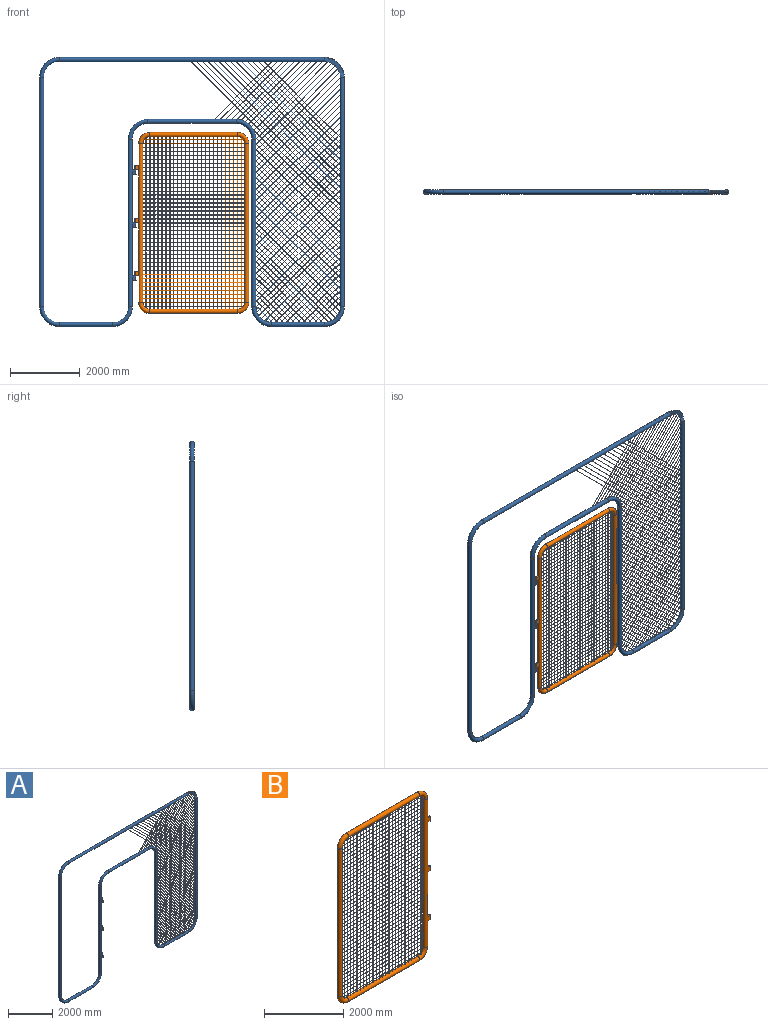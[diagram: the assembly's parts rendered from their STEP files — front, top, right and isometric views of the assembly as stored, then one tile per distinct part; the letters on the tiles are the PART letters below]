
ASSEMBLY  parts=2 mates=1
PART A: 186 faces, bbox 8852.5x122.7x7836.5 mm
  f0: torus R=508mm, axis (0,-1,0), area 307549mm2, adj f1,f15
  f1: cylinder r=61.34mm len=1524mm, axis (1,0,0), area 587375.3mm2, adj f0,f2
  f2: torus R=508mm, axis (0,-1,0), area 307549mm2, adj f1,f3
  f3: cylinder r=61.34mm len=6604mm, axis (0,0,-1), area 2545293mm2, adj f2,f4
  f4: torus R=508mm, axis (0,-1,0), area 307549mm2, adj f3,f5
  f5: cylinder r=61.34mm len=7620mm, axis (-1,0,0), area 2935875.4mm2, adj f4,f6,f47,f48,f49,f50,f51,f52
  f6: torus R=508mm, axis (0,-1,0), area 307392.8mm2, adj f5,f7,f103,f104,f105,f106,f107
  f7: cylinder r=61.34mm len=6604mm, axis (0,0,1), area 2542310.5mm2, adj f6,f8,f30,f31,f32,f33,f34,f35
  f8: torus R=508mm, axis (0,-1,0), area 307391.4mm2, adj f7,f9,f25,f26,f27,f28,f29
  f9: cylinder r=61.34mm len=1524mm, axis (1,0,0), area 586591mm2, adj f8,f10,f16,f17,f18,f19,f20,f21
  f10: torus R=508mm, axis (0,-1,0), area 307350.3mm2, adj f9,f11,f62,f63,f64,f65,f66,f76
  f11: cylinder r=61.34mm len=4826mm, axis (0,0,-1), area 1857540.3mm2, adj f10,f12,f16,f17,f18,f19,f20,f21
  f12: torus R=508mm, axis (0,1,0), area 307176.7mm2, adj f11,f13,f45,f46,f107,f108,f109,f110
  f13: cylinder r=61.34mm len=2540mm, axis (1,0,0), area 978792.6mm2, adj f12,f14,f114,f115,f116,f117
  f14: torus R=508mm, axis (0,1,0), area 307549mm2, adj f13,f15
  f15: cylinder r=61.34mm len=4826mm, axis (0,0,1), area 1840066.3mm2, adj f0,f14,f118,f119,f120,f121,f124,f125
  f16: cylinder r=3.05mm len=640.63mm, axis (-0.71,0,0.71), area 17118.8mm2, adj f9,f11
  f17: cylinder r=3.05mm len=801.92mm, axis (-0.71,0,0.71), area 21487.2mm2, adj f9,f11
  f18: cylinder r=3.05mm len=963.21mm, axis (-0.71,0,0.71), area 25855.5mm2, adj f9,f11
  f19: cylinder r=3.05mm len=1124.5mm, axis (-0.71,0,0.71), area 30223.9mm2, adj f9,f11
  f20: cylinder r=3.05mm len=1285.79mm, axis (-0.71,0,0.71), area 34592.2mm2, adj f9,f11
  f21: cylinder r=3.05mm len=1447.08mm, axis (-0.71,0,0.71), area 38960.6mm2, adj f9,f11
  f22: cylinder r=3.05mm len=1608.37mm, axis (-0.71,0,0.71), area 43328.9mm2, adj f9,f11
  f23: cylinder r=3.05mm len=1769.66mm, axis (-0.71,0,0.71), area 47697.3mm2, adj f9,f11
  f24: cylinder r=3.05mm len=1930.95mm, axis (-0.71,0,0.71), area 52065.6mm2, adj f9,f11
  f25: cylinder r=3.05mm len=2079.79mm, axis (-0.71,0,0.71), area 56118.8mm2, adj f8,f11
  f26: cylinder r=3.05mm len=2195.41mm, axis (-0.71,0,0.71), area 59269.8mm2, adj f8,f11
  f27: cylinder r=3.05mm len=2287.57mm, axis (-0.71,0,0.71), area 61777.9mm2, adj f8,f11
  f28: cylinder r=3.05mm len=2359.6mm, axis (-0.71,0,0.71), area 63718.8mm2, adj f8,f11
  f29: cylinder r=3.05mm len=2408.95mm, axis (-0.71,0,0.71), area 65037.1mm2, adj f8,f11
  f30: cylinder r=3.05mm len=2426.1mm, axis (-0.71,0,0.71), area 65476.3mm2, adj f7,f11
  f31: cylinder r=3.05mm len=2426.1mm, axis (-0.71,0,0.71), area 65476.3mm2, adj f7,f11
  f32: cylinder r=3.05mm len=2426.1mm, axis (-0.71,0,0.71), area 65476.3mm2, adj f7,f11
  f33: cylinder r=3.05mm len=2426.1mm, axis (-0.71,0,0.71), area 65476.3mm2, adj f7,f11
  f34: cylinder r=3.05mm len=2426.1mm, axis (-0.71,0,0.71), area 65476.3mm2, adj f7,f11
  f35: cylinder r=3.05mm len=2426.1mm, axis (-0.71,0,0.71), area 65476.3mm2, adj f7,f11
  f36: cylinder r=3.05mm len=2426.1mm, axis (-0.71,0,0.71), area 65476.3mm2, adj f7,f11
  f37: cylinder r=3.05mm len=2426.1mm, axis (-0.71,0,0.71), area 65476.3mm2, adj f7,f11
  f38: cylinder r=3.05mm len=2426.1mm, axis (-0.71,0,0.71), area 65476.3mm2, adj f7,f11
  f39: cylinder r=3.05mm len=2426.1mm, axis (-0.71,0,0.71), area 65476.3mm2, adj f7,f11
  f40: cylinder r=3.05mm len=2426.1mm, axis (-0.71,0,0.71), area 65476.3mm2, adj f7,f11
  f41: cylinder r=3.05mm len=2426.1mm, axis (-0.71,0,0.71), area 65476.3mm2, adj f7,f11
  f42: cylinder r=3.05mm len=2426.1mm, axis (-0.71,0,0.71), area 65476.3mm2, adj f7,f11
  f43: cylinder r=3.05mm len=2426.1mm, axis (-0.71,0,0.71), area 65476.3mm2, adj f7,f11
  f44: cylinder r=3.05mm len=2426.1mm, axis (-0.71,0,0.71), area 65476.3mm2, adj f7,f11
  f45: cylinder r=3.05mm len=2427.7mm, axis (-0.71,0,0.71), area 65511mm2, adj f7,f12
  f46: cylinder r=3.05mm len=2494.65mm, axis (-0.71,0,0.71), area 67205.7mm2, adj f7,f12
  f47: cylinder r=3.05mm len=4291.59mm, axis (-0.71,0,0.71), area 116000.9mm2, adj f5,f7
  f48: cylinder r=3.05mm len=4130.3mm, axis (-0.71,0,0.71), area 111632.5mm2, adj f5,f7
  f49: cylinder r=3.05mm len=3969.01mm, axis (-0.71,0,0.71), area 107264.2mm2, adj f5,f7
  f50: cylinder r=3.05mm len=3807.72mm, axis (-0.71,0,0.71), area 102895.8mm2, adj f5,f7
  f51: cylinder r=3.05mm len=3646.43mm, axis (-0.71,0,0.71), area 98527.5mm2, adj f5,f7
  f52: cylinder r=3.05mm len=3485.14mm, axis (-0.71,0,0.71), area 94159.1mm2, adj f5,f7
  f53: cylinder r=3.05mm len=3323.85mm, axis (-0.71,0,0.71), area 89790.8mm2, adj f5,f7
  f54: cylinder r=3.05mm len=3162.56mm, axis (-0.71,0,0.71), area 85422.4mm2, adj f5,f7
  f55: cylinder r=3.05mm len=3001.27mm, axis (-0.71,0,0.71), area 81054.1mm2, adj f5,f7
  f56: cylinder r=3.05mm len=2839.98mm, axis (-0.71,0,0.71), area 76685.7mm2, adj f5,f7
  f57: cylinder r=3.05mm len=2678.69mm, axis (-0.71,0,0.71), area 72317.4mm2, adj f5,f7
  f58: cylinder r=3.05mm len=2517.4mm, axis (-0.71,0,0.71), area 67949mm2, adj f5,f7
  f59: cylinder r=3.05mm len=2356.11mm, axis (-0.71,0,0.71), area 63580.7mm2, adj f5,f7
  f60: cylinder r=3.05mm len=2194.82mm, axis (-0.71,0,0.71), area 59212.3mm2, adj f5,f7
  f61: cylinder r=3.05mm len=479.34mm, axis (-0.71,0,0.71), area 12750.5mm2, adj f9,f11
  f62: cylinder r=3.05mm len=2396.51mm, axis (-0.71,0,-0.71), area 64706.6mm2, adj f7,f10
  f63: cylinder r=3.05mm len=2339.58mm, axis (-0.71,0,-0.71), area 63181.2mm2, adj f7,f10
  f64: cylinder r=3.05mm len=2261.34mm, axis (-0.71,0,-0.71), area 61065.2mm2, adj f7,f10
  f65: cylinder r=3.05mm len=2162.52mm, axis (-0.71,0,-0.71), area 58373.6mm2, adj f7,f10
  f66: cylinder r=3.05mm len=2038mm, axis (-0.71,0,-0.71), area 54978.7mm2, adj f7,f10
  f67: cylinder r=3.05mm len=1881.16mm, axis (-0.71,0,-0.71), area 50717.1mm2, adj f7,f9
  f68: cylinder r=3.05mm len=1719.87mm, axis (-0.71,0,-0.71), area 46348.7mm2, adj f7,f9
  f69: cylinder r=3.05mm len=1558.58mm, axis (-0.71,0,-0.71), area 41980.4mm2, adj f7,f9
  f70: cylinder r=3.05mm len=1397.29mm, axis (-0.71,0,-0.71), area 37612mm2, adj f7,f9
  f71: cylinder r=3.05mm len=1236mm, axis (-0.71,0,-0.71), area 33243.7mm2, adj f7,f9
  f72: cylinder r=3.05mm len=1074.71mm, axis (-0.71,0,-0.71), area 28875.4mm2, adj f7,f9
  f73: cylinder r=3.05mm len=913.42mm, axis (-0.71,0,-0.71), area 24507mm2, adj f7,f9
  f74: cylinder r=3.05mm len=752.13mm, axis (-0.71,0,-0.71), area 20138.7mm2, adj f7,f9
  f75: cylinder r=3.05mm len=590.84mm, axis (-0.71,0,-0.71), area 15770.3mm2, adj f7,f9
  f76: cylinder r=3.05mm len=2425.29mm, axis (-0.71,0,-0.71), area 65460.2mm2, adj f7,f10
  f77: cylinder r=3.05mm len=2426.13mm, axis (-0.71,0,-0.71), area 65477.1mm2, adj f7,f11
  f78: cylinder r=3.05mm len=2426.13mm, axis (-0.71,0,-0.71), area 65477.1mm2, adj f7,f11
  f79: cylinder r=3.05mm len=2426.13mm, axis (-0.71,0,-0.71), area 65477.1mm2, adj f7,f11
  f80: cylinder r=3.05mm len=2426.13mm, axis (-0.71,0,-0.71), area 65477.1mm2, adj f7,f11
  f81: cylinder r=3.05mm len=2426.13mm, axis (-0.71,0,-0.71), area 65477.1mm2, adj f7,f11
  f82: cylinder r=3.05mm len=2426.13mm, axis (-0.71,0,-0.71), area 65477.1mm2, adj f7,f11
  f83: cylinder r=3.05mm len=2426.13mm, axis (-0.71,0,-0.71), area 65477.1mm2, adj f7,f11
  f84: cylinder r=3.05mm len=2426.13mm, axis (-0.71,0,-0.71), area 65477.1mm2, adj f7,f11
  f85: cylinder r=3.05mm len=2426.13mm, axis (-0.71,0,-0.71), area 65477.1mm2, adj f7,f11
  f86: cylinder r=3.05mm len=2426.13mm, axis (-0.71,0,-0.71), area 65477.1mm2, adj f7,f11
  f87: cylinder r=3.05mm len=2426.13mm, axis (-0.71,0,-0.71), area 65477.1mm2, adj f7,f11
  f88: cylinder r=3.05mm len=2426.13mm, axis (-0.71,0,-0.71), area 65477.1mm2, adj f7,f11
  f89: cylinder r=3.05mm len=2426.13mm, axis (-0.71,0,-0.71), area 65477.1mm2, adj f7,f11
  f90: cylinder r=3.05mm len=2426.13mm, axis (-0.71,0,-0.71), area 65477.1mm2, adj f7,f11
  f91: cylinder r=3.05mm len=2426.13mm, axis (-0.71,0,-0.71), area 65477.1mm2, adj f7,f11
  f92: cylinder r=3.05mm len=2426.13mm, axis (-0.71,0,-0.71), area 65477.1mm2, adj f7,f11
  f93: cylinder r=3.05mm len=2426.13mm, axis (-0.71,0,-0.71), area 65477.1mm2, adj f7,f11
  f94: cylinder r=3.05mm len=2426.13mm, axis (-0.71,0,-0.71), area 65477.1mm2, adj f7,f11
  f95: cylinder r=3.05mm len=2426.13mm, axis (-0.71,0,-0.71), area 65477.1mm2, adj f7,f11
  f96: cylinder r=3.05mm len=2426.13mm, axis (-0.71,0,-0.71), area 65477.1mm2, adj f7,f11
  f97: cylinder r=3.05mm len=2426.13mm, axis (-0.71,0,-0.71), area 65477.1mm2, adj f7,f11
  f98: cylinder r=3.05mm len=2426.13mm, axis (-0.71,0,-0.71), area 65477.1mm2, adj f7,f11
  f99: cylinder r=3.05mm len=2426.13mm, axis (-0.71,0,-0.71), area 65477.1mm2, adj f7,f11
  f100: cylinder r=3.05mm len=2426.13mm, axis (-0.71,0,-0.71), area 65477.1mm2, adj f7,f11
  f101: cylinder r=3.05mm len=2426.13mm, axis (-0.71,0,-0.71), area 65477.1mm2, adj f7,f11
  f102: cylinder r=3.05mm len=2426.13mm, axis (-0.71,0,-0.71), area 65477.1mm2, adj f7,f11
  f103: cylinder r=3.05mm len=2406.96mm, axis (-0.71,0,-0.71), area 64984.2mm2, adj f6,f11
  f104: cylinder r=3.05mm len=2356.2mm, axis (-0.71,0,-0.71), area 63627.6mm2, adj f6,f11
  f105: cylinder r=3.05mm len=2283.05mm, axis (-0.71,0,-0.71), area 61655.2mm2, adj f6,f11
  f106: cylinder r=3.05mm len=2189.73mm, axis (-0.71,0,-0.71), area 59114.9mm2, adj f6,f11
  f107: cylinder r=3.05mm len=2087.77mm, axis (-0.71,0,-0.71), area 56356mm2, adj f6,f12
  f108: cylinder r=3.05mm len=1979.65mm, axis (-0.71,0,-0.71), area 53422.7mm2, adj f5,f12
  f109: cylinder r=3.05mm len=1880.25mm, axis (-0.71,0,-0.71), area 50742.6mm2, adj f5,f12
  f110: cylinder r=3.05mm len=1797.92mm, axis (-0.71,0,-0.71), area 48514.9mm2, adj f5,f12
  f111: cylinder r=3.05mm len=1732.57mm, axis (-0.71,0,-0.71), area 46733.4mm2, adj f5,f12
  f112: cylinder r=3.05mm len=1685.9mm, axis (-0.71,0,-0.71), area 45455.1mm2, adj f5,f12
  f113: cylinder r=3.05mm len=1664.36mm, axis (-0.71,0,-0.71), area 44849.3mm2, adj f5,f12
  f114: cylinder r=3.05mm len=1664.13mm, axis (-0.71,0,-0.71), area 44839.2mm2, adj f5,f13
  f115: cylinder r=3.05mm len=1664.13mm, axis (-0.71,0,-0.71), area 44839.2mm2, adj f5,f13
  f116: cylinder r=3.05mm len=1664.13mm, axis (-0.71,0,-0.71), area 44839.2mm2, adj f5,f13
  f117: cylinder r=3.05mm len=1664.13mm, axis (-0.71,0,-0.71), area 44839.2mm2, adj f5,f13
  f118: plane 121.97x50.8mm, normal (0,0,-1), area 5730.7mm2, adj f15,f119,f121,f138
  f119: plane 127x96.57mm, normal (0,1,0), area 12263.7mm2, adj f15,f118,f120,f138
  f120: plane 121.97x50.8mm, normal (0,0,1), area 5406.4mm2, adj f15,f119,f121,f122,f138
  f121: plane 127x96.57mm, normal (0,-1,0), area 12263.7mm2, adj f15,f118,f120,f138
  f122: cylinder r=10.16mm len=127mm, axis (0,0,-1), area 8107.3mm2, adj f120,f123
  f123: plane 20.32x20.32mm, normal (0,0,1), area 324.3mm2, adj f122
  f124: plane 121.97x50.8mm, normal (0,0,-1), area 5730.7mm2, adj f15,f125,f127,f128
  f125: plane 127x96.57mm, normal (0,1,0), area 12263.7mm2, adj f15,f124,f126,f128
  f126: plane 121.97x50.8mm, normal (0,0,1), area 5406.4mm2, adj f15,f125,f127,f128,f129
  f127: plane 127x96.57mm, normal (0,-1,0), area 12263.7mm2, adj f15,f124,f126,f128
  f128: cylinder r=25.4mm len=127mm, axis (0,0,1), area 10134.1mm2, adj f124,f125,f126,f127
  f129: cylinder r=10.16mm len=127mm, axis (0,0,-1), area 8107.3mm2, adj f126,f130
  f130: plane 20.32x20.32mm, normal (0,0,1), area 324.3mm2, adj f129
  f131: plane 121.97x50.8mm, normal (0,0,-1), area 5730.7mm2, adj f15,f132,f134,f135
  f132: plane 127x96.57mm, normal (0,1,0), area 12263.7mm2, adj f15,f131,f133,f135
  f133: plane 121.97x50.8mm, normal (0,0,1), area 5406.4mm2, adj f15,f132,f134,f135,f136
  f134: plane 127x96.57mm, normal (0,-1,0), area 12263.7mm2, adj f15,f131,f133,f135
  f135: cylinder r=25.4mm len=127mm, axis (0,0,1), area 10134.1mm2, adj f131,f132,f133,f134
  f136: cylinder r=10.16mm len=127mm, axis (0,0,-1), area 8107.3mm2, adj f133,f137
  f137: plane 20.32x20.32mm, normal (0,0,1), area 324.3mm2, adj f136
  f138: cylinder r=25.4mm len=127mm, axis (0,0,1), area 10134.1mm2, adj f118,f119,f120,f121
  f139: torus R=508mm, axis (0,-1,0), area 282079.1mm2, adj f140,f154
  f140: cylinder r=56.26mm len=1524mm, axis (1,0,0), area 538731.4mm2, adj f139,f141
  f141: torus R=508mm, axis (0,-1,0), area 282079.1mm2, adj f140,f142
  f142: cylinder r=56.26mm len=6604mm, axis (0,0,-1), area 2334502.7mm2, adj f141,f143
  f143: torus R=508mm, axis (0,-1,0), area 282079.1mm2, adj f142,f144
  f144: cylinder r=56.26mm len=7620mm, axis (-1,0,0), area 2692702.4mm2, adj f143,f145,f155,f158,f159,f160,f161,f162
  f145: torus R=508mm, axis (0,-1,0), area 281782.3mm2, adj f144,f146,f156,f157,f168,f169,f170
  f146: cylinder r=56.26mm len=6604mm, axis (0,0,1), area 2334502.7mm2, adj f145,f147
  f147: torus R=508mm, axis (0,-1,0), area 282079.1mm2, adj f146,f148
  f148: cylinder r=56.26mm len=1524mm, axis (1,0,0), area 538731.4mm2, adj f147,f149
  f149: torus R=508mm, axis (0,-1,0), area 282079.1mm2, adj f148,f150
  f150: cylinder r=56.26mm len=4826mm, axis (0,0,-1), area 1705982.7mm2, adj f149,f151
  f151: torus R=508mm, axis (0,1,0), area 282079.1mm2, adj f150,f152
  f152: cylinder r=56.26mm len=2540mm, axis (1,0,0), area 897885.7mm2, adj f151,f153
  f153: torus R=508mm, axis (0,1,0), area 282079.1mm2, adj f152,f154
  f154: cylinder r=56.26mm len=4826mm, axis (0,0,1), area 1685901.6mm2, adj f139,f153,f172,f173,f174,f175,f177,f178
  f155: cylinder r=3.05mm len=120.99mm, axis (-0.71,0,0.71), area 3040.8mm2, adj f144
  f156: cylinder r=3.05mm len=94.08mm, axis (-0.71,0,-0.71), area 2373.7mm2, adj f145
  f157: cylinder r=3.05mm len=86.24mm, axis (-0.71,0,-0.71), area 2192.9mm2, adj f145
  f158: cylinder r=3.05mm len=120.96mm, axis (-0.71,0,-0.71), area 3040mm2, adj f144
  f159: cylinder r=3.05mm len=120.96mm, axis (-0.71,0,-0.71), area 3040mm2, adj f144
  f160: cylinder r=3.05mm len=120.96mm, axis (-0.71,0,-0.71), area 3040mm2, adj f144
  f161: cylinder r=3.05mm len=120.96mm, axis (-0.71,0,-0.71), area 3040mm2, adj f144
  f162: cylinder r=3.05mm len=120.96mm, axis (-0.71,0,-0.71), area 3040mm2, adj f144
  f163: cylinder r=3.05mm len=120.96mm, axis (-0.71,0,-0.71), area 3040mm2, adj f144
  f164: cylinder r=3.05mm len=120.96mm, axis (-0.71,0,-0.71), area 3040mm2, adj f144
  f165: cylinder r=3.05mm len=120.96mm, axis (-0.71,0,-0.71), area 3040mm2, adj f144
  f166: cylinder r=3.05mm len=120.96mm, axis (-0.71,0,-0.71), area 3040mm2, adj f144
  f167: cylinder r=3.05mm len=120.96mm, axis (-0.71,0,-0.71), area 3040mm2, adj f144
  f168: cylinder r=3.05mm len=117.65mm, axis (-0.71,0,-0.71), area 2961.2mm2, adj f144,f145
  f169: cylinder r=3.05mm len=97.32mm, axis (-0.71,0,-0.71), area 2451.8mm2, adj f145
  f170: cylinder r=3.05mm len=87.61mm, axis (-0.71,0,-0.71), area 2222.7mm2, adj f145
  f171: plane 127x50.8mm, normal (-1,0,0), area 6451.6mm2, adj f172,f173,f174,f175
  f172: plane 127x50.2mm, normal (0,-1,0), area 6375.5mm2, adj f154,f171,f173,f175
  f173: plane 56.26x50.8mm, normal (0,0,1), area 2757.8mm2, adj f154,f171,f172,f174
  f174: plane 127x50.2mm, normal (0,1,0), area 6375.5mm2, adj f154,f171,f173,f175
  f175: plane 56.26x50.8mm, normal (0,0,-1), area 2757.8mm2, adj f154,f171,f172,f174
  f176: plane 127x50.8mm, normal (-1,0,0), area 6451.6mm2, adj f177,f178,f179,f180
  f177: plane 127x50.2mm, normal (0,-1,0), area 6375.5mm2, adj f154,f176,f178,f180
  f178: plane 56.26x50.8mm, normal (0,0,1), area 2757.8mm2, adj f154,f176,f177,f179
  f179: plane 127x50.2mm, normal (0,1,0), area 6375.5mm2, adj f154,f176,f178,f180
  f180: plane 56.26x50.8mm, normal (0,0,-1), area 2757.8mm2, adj f154,f176,f177,f179
  f181: plane 127x50.8mm, normal (-1,0,0), area 6451.6mm2, adj f182,f183,f184,f185
  f182: plane 127x50.2mm, normal (0,-1,0), area 6375.5mm2, adj f154,f181,f183,f185
  f183: plane 56.26x50.8mm, normal (0,0,1), area 2757.8mm2, adj f154,f181,f182,f184
  f184: plane 127x50.2mm, normal (0,1,0), area 6375.5mm2, adj f154,f181,f183,f185
  f185: plane 56.26x50.8mm, normal (0,0,-1), area 2757.8mm2, adj f154,f181,f182,f184
PART B: 125 faces, bbox 3313.1x122.7x5254.6 mm
  f0: cylinder r=61.34mm len=4572mm, axis (0,0,-1), area 1741001mm2, adj f2,f3,f33,f34,f35,f36,f37,f38
  f1: torus R=254mm, axis (0,1,0), area 153689.5mm2, adj f5,f7,f32,f74,f75
  f2: torus R=254mm, axis (0,1,0), area 153690.2mm2, adj f0,f5,f20,f74,f75
  f3: torus R=254mm, axis (0,1,0), area 153689mm2, adj f0,f6,f20,f53,f54
  f4: torus R=254mm, axis (0,1,0), area 153688.4mm2, adj f6,f7,f32,f53,f54
  f5: cylinder r=61.34mm len=2540mm, axis (-1,0,0), area 978283.2mm2, adj f1,f2,f8,f9,f10,f11,f12,f13
  f6: cylinder r=61.34mm len=2540mm, axis (1,0,0), area 978298.7mm2, adj f3,f4,f8,f9,f10,f11,f12,f13
  f7: cylinder r=61.34mm len=4572mm, axis (0,0,1), area 1760956.1mm2, adj f1,f4,f33,f34,f35,f36,f37,f38
  f8: cylinder r=3.05mm len=4957.93mm, axis (0,0,-1), area 94942.7mm2, adj f5,f6
  f9: cylinder r=3.05mm len=4957.93mm, axis (0,0,-1), area 94942.7mm2, adj f5,f6
  f10: cylinder r=3.05mm len=4957.93mm, axis (0,0,-1), area 94942.7mm2, adj f5,f6
  f11: cylinder r=3.05mm len=4957.93mm, axis (0,0,-1), area 94942.7mm2, adj f5,f6
  f12: cylinder r=3.05mm len=4957.93mm, axis (0,0,-1), area 94942.7mm2, adj f5,f6
  f13: cylinder r=3.05mm len=4957.93mm, axis (0,0,-1), area 94942.7mm2, adj f5,f6
  f14: cylinder r=3.05mm len=4957.93mm, axis (0,0,-1), area 94942.7mm2, adj f5,f6
  f15: cylinder r=3.05mm len=4957.93mm, axis (0,0,-1), area 94942.7mm2, adj f5,f6
  f16: cylinder r=3.05mm len=4957.93mm, axis (0,0,-1), area 94942.7mm2, adj f5,f6
  f17: cylinder r=3.05mm len=4957.93mm, axis (0,0,-1), area 94942.7mm2, adj f5,f6
  f18: cylinder r=3.05mm len=4957.93mm, axis (0,0,-1), area 94942.7mm2, adj f5,f6
  f19: cylinder r=3.05mm len=4957.93mm, axis (0,0,-1), area 94942.7mm2, adj f5,f6
  f20: cylinder r=3.05mm len=4903.29mm, axis (0,0,-1), area 93833.2mm2, adj f2,f3
  f21: cylinder r=3.05mm len=4957.93mm, axis (0,0,-1), area 94942.7mm2, adj f5,f6
  f22: cylinder r=3.05mm len=4957.93mm, axis (0,0,-1), area 94942.7mm2, adj f5,f6
  f23: cylinder r=3.05mm len=4957.93mm, axis (0,0,-1), area 94942.7mm2, adj f5,f6
  f24: cylinder r=3.05mm len=4957.93mm, axis (0,0,-1), area 94942.7mm2, adj f5,f6
  f25: cylinder r=3.05mm len=4957.93mm, axis (0,0,-1), area 94942.7mm2, adj f5,f6
  f26: cylinder r=3.05mm len=4957.93mm, axis (0,0,-1), area 94942.7mm2, adj f5,f6
  f27: cylinder r=3.05mm len=4957.93mm, axis (0,0,-1), area 94942.7mm2, adj f5,f6
  f28: cylinder r=3.05mm len=4957.93mm, axis (0,0,-1), area 94942.7mm2, adj f5,f6
  f29: cylinder r=3.05mm len=4957.93mm, axis (0,0,-1), area 94942.7mm2, adj f5,f6
  f30: cylinder r=3.05mm len=4957.93mm, axis (0,0,-1), area 94942.7mm2, adj f5,f6
  f31: cylinder r=3.05mm len=4957.93mm, axis (0,0,-1), area 94942.7mm2, adj f5,f6
  f32: cylinder r=3.05mm len=4903.29mm, axis (0,0,-1), area 93833.2mm2, adj f1,f4
  f33: cylinder r=3.05mm len=2925.98mm, axis (-1,0,0), area 56028.1mm2, adj f0,f7
  f34: cylinder r=3.05mm len=2925.98mm, axis (-1,0,0), area 56028.1mm2, adj f0,f7
  f35: cylinder r=3.05mm len=2925.98mm, axis (-1,0,0), area 56028.1mm2, adj f0,f7
  f36: cylinder r=3.05mm len=2925.98mm, axis (-1,0,0), area 56028.1mm2, adj f0,f7
  f37: cylinder r=3.05mm len=2925.98mm, axis (-1,0,0), area 56028.1mm2, adj f0,f7
  f38: cylinder r=3.05mm len=2925.98mm, axis (-1,0,0), area 56028.1mm2, adj f0,f7
  f39: cylinder r=3.05mm len=2925.98mm, axis (-1,0,0), area 56028.1mm2, adj f0,f7
  f40: cylinder r=3.05mm len=2925.98mm, axis (-1,0,0), area 56028.1mm2, adj f0,f7
  f41: cylinder r=3.05mm len=2925.98mm, axis (-1,0,0), area 56028.1mm2, adj f0,f7
  f42: cylinder r=3.05mm len=2925.98mm, axis (-1,0,0), area 56028.1mm2, adj f0,f7
  f43: cylinder r=3.05mm len=2925.98mm, axis (-1,0,0), area 56028.1mm2, adj f0,f7
  f44: cylinder r=3.05mm len=2925.98mm, axis (-1,0,0), area 56028.1mm2, adj f0,f7
  f45: cylinder r=3.05mm len=2925.98mm, axis (-1,0,0), area 56028.1mm2, adj f0,f7
  f46: cylinder r=3.05mm len=2925.98mm, axis (-1,0,0), area 56028.1mm2, adj f0,f7
  f47: cylinder r=3.05mm len=2925.98mm, axis (-1,0,0), area 56028.1mm2, adj f0,f7
  f48: cylinder r=3.05mm len=2925.98mm, axis (-1,0,0), area 56028.1mm2, adj f0,f7
  f49: cylinder r=3.05mm len=2925.98mm, axis (-1,0,0), area 56028.1mm2, adj f0,f7
  f50: cylinder r=3.05mm len=2925.98mm, axis (-1,0,0), area 56028.1mm2, adj f0,f7
  f51: cylinder r=3.05mm len=2925.98mm, axis (-1,0,0), area 56028.1mm2, adj f0,f7
  f52: cylinder r=3.05mm len=2925.98mm, axis (-1,0,0), area 56028.1mm2, adj f0,f7
  f53: cylinder r=3.05mm len=2925.98mm, axis (-1,0,0), area 56027.8mm2, adj f0,f3,f4,f7
  f54: cylinder r=3.05mm len=2854.82mm, axis (-1,0,0), area 54589.4mm2, adj f3,f4
  f55: cylinder r=3.05mm len=2925.98mm, axis (-1,0,0), area 56028.1mm2, adj f0,f7
  f56: cylinder r=3.05mm len=2925.98mm, axis (-1,0,0), area 56028.1mm2, adj f0,f7
  f57: cylinder r=3.05mm len=2925.98mm, axis (-1,0,0), area 56028.1mm2, adj f0,f7
  f58: cylinder r=3.05mm len=2925.98mm, axis (-1,0,0), area 56028.1mm2, adj f0,f7
  f59: cylinder r=3.05mm len=2925.98mm, axis (-1,0,0), area 56028.1mm2, adj f0,f7
  f60: cylinder r=3.05mm len=2925.98mm, axis (-1,0,0), area 56028.1mm2, adj f0,f7
  f61: cylinder r=3.05mm len=2925.98mm, axis (-1,0,0), area 56028.1mm2, adj f0,f7
  f62: cylinder r=3.05mm len=2925.98mm, axis (-1,0,0), area 56028.1mm2, adj f0,f7
  f63: cylinder r=3.05mm len=2925.98mm, axis (-1,0,0), area 56028.1mm2, adj f0,f7
  f64: cylinder r=3.05mm len=2925.98mm, axis (-1,0,0), area 56028.1mm2, adj f0,f7
  f65: cylinder r=3.05mm len=2925.98mm, axis (-1,0,0), area 56028.1mm2, adj f0,f7
  f66: cylinder r=3.05mm len=2925.98mm, axis (-1,0,0), area 56028.1mm2, adj f0,f7
  f67: cylinder r=3.05mm len=2925.98mm, axis (-1,0,0), area 56028.1mm2, adj f0,f7
  f68: cylinder r=3.05mm len=2925.98mm, axis (-1,0,0), area 56028.1mm2, adj f0,f7
  f69: cylinder r=3.05mm len=2925.98mm, axis (-1,0,0), area 56028.1mm2, adj f0,f7
  f70: cylinder r=3.05mm len=2925.98mm, axis (-1,0,0), area 56028.1mm2, adj f0,f7
  f71: cylinder r=3.05mm len=2925.98mm, axis (-1,0,0), area 56028.1mm2, adj f0,f7
  f72: cylinder r=3.05mm len=2925.98mm, axis (-1,0,0), area 56028.1mm2, adj f0,f7
  f73: cylinder r=3.05mm len=2925.98mm, axis (-1,0,0), area 56028.1mm2, adj f0,f7
  f74: cylinder r=3.05mm len=2925.98mm, axis (-1,0,0), area 56027.8mm2, adj f0,f1,f2,f7
  f75: cylinder r=3.05mm len=2854.82mm, axis (-1,0,0), area 54589.4mm2, adj f1,f2
  f76: plane 127x96.57mm, normal (0,-1,0), area 12263.7mm2, adj f0,f77,f79,f92
  f77: plane 121.97x50.8mm, normal (0,0,-1), area 5406.4mm2, adj f0,f76,f78,f92,f93
  f78: plane 127x96.57mm, normal (0,1,0), area 12263.7mm2, adj f0,f77,f79,f92
  f79: plane 121.97x50.8mm, normal (0,0,1), area 5406.4mm2, adj f0,f76,f78,f92,f93
  f80: plane 127x96.57mm, normal (0,-1,0), area 12263.7mm2, adj f0,f81,f83,f84
  f81: plane 121.97x50.8mm, normal (0,0,-1), area 5406.4mm2, adj f0,f80,f82,f84,f85
  f82: plane 127x96.57mm, normal (0,1,0), area 12263.7mm2, adj f0,f81,f83,f84
  f83: plane 121.97x50.8mm, normal (0,0,1), area 5406.4mm2, adj f0,f80,f82,f84,f85
  f84: cylinder r=25.4mm len=127mm, axis (0,0,1), area 10134.1mm2, adj f80,f81,f82,f83
  f85: cylinder r=10.16mm len=127mm, axis (0,0,1), area 8107.3mm2, adj f81,f83
  f86: plane 127x96.57mm, normal (0,-1,0), area 12263.7mm2, adj f0,f87,f89,f90
  f87: plane 121.97x50.8mm, normal (0,0,-1), area 5406.4mm2, adj f0,f86,f88,f90,f91
  f88: plane 127x96.57mm, normal (0,1,0), area 12263.7mm2, adj f0,f87,f89,f90
  f89: plane 121.97x50.8mm, normal (0,0,1), area 5406.4mm2, adj f0,f86,f88,f90,f91
  f90: cylinder r=25.4mm len=127mm, axis (0,0,1), area 10134.1mm2, adj f86,f87,f88,f89
  f91: cylinder r=10.16mm len=127mm, axis (0,0,1), area 8107.3mm2, adj f87,f89
  f92: cylinder r=25.4mm len=127mm, axis (0,0,1), area 10134.1mm2, adj f76,f77,f78,f79
  f93: cylinder r=10.16mm len=127mm, axis (0,0,1), area 8107.3mm2, adj f77,f79
  f94: cylinder r=56.26mm len=4572mm, axis (0,0,-1), area 1596113.1mm2, adj f96,f97,f111,f112,f113,f114,f116,f117
  f95: torus R=254mm, axis (0,1,0), area 141004mm2, adj f99,f101,f109
  f96: torus R=254mm, axis (0,1,0), area 141003.8mm2, adj f94,f99,f107
  f97: torus R=254mm, axis (0,1,0), area 141003.7mm2, adj f94,f100,f105
  f98: torus R=254mm, axis (0,1,0), area 141003.7mm2, adj f100,f101,f103
  f99: cylinder r=56.26mm len=2540mm, axis (-1,0,0), area 897885.7mm2, adj f95,f96
  f100: cylinder r=56.26mm len=2540mm, axis (1,0,0), area 897885.7mm2, adj f97,f98
  f101: cylinder r=56.26mm len=4572mm, axis (0,0,1), area 1616194.2mm2, adj f95,f98
  f102: cylinder r=61.34mm len=6.1mm, axis (0,0,1), area 29.2mm2, adj f103
  f103: cylinder r=3.05mm len=33.72mm, axis (-1,0,0), area 599.1mm2, adj f98,f102
  f104: cylinder r=61.34mm len=6.1mm, axis (0,0,-1), area 29.2mm2, adj f105
  f105: cylinder r=3.05mm len=33.72mm, axis (-1,0,0), area 599.1mm2, adj f97,f104
  f106: cylinder r=61.34mm len=6.1mm, axis (0,0,-1), area 29.2mm2, adj f107
  f107: cylinder r=3.05mm len=33.72mm, axis (-1,0,0), area 599.1mm2, adj f96,f106
  f108: cylinder r=61.34mm len=6.1mm, axis (0,0,1), area 29.2mm2, adj f109
  f109: cylinder r=3.05mm len=33.72mm, axis (-1,0,0), area 599.1mm2, adj f95,f108
  f110: plane 127x50.8mm, normal (-1,0,0), area 6451.6mm2, adj f111,f112,f113,f114
  f111: plane 56.26x50.8mm, normal (0,0,1), area 2757.8mm2, adj f94,f110,f112,f114
  f112: plane 127x50.2mm, normal (0,1,0), area 6375.5mm2, adj f94,f110,f111,f113
  f113: plane 56.26x50.8mm, normal (0,0,-1), area 2757.8mm2, adj f94,f110,f112,f114
  f114: plane 127x50.2mm, normal (0,-1,0), area 6375.5mm2, adj f94,f110,f111,f113
  f115: plane 127x50.8mm, normal (-1,0,0), area 6451.6mm2, adj f116,f117,f118,f119
  f116: plane 56.26x50.8mm, normal (0,0,1), area 2757.8mm2, adj f94,f115,f117,f119
  f117: plane 127x50.2mm, normal (0,1,0), area 6375.5mm2, adj f94,f115,f116,f118
  f118: plane 56.26x50.8mm, normal (0,0,-1), area 2757.8mm2, adj f94,f115,f117,f119
  f119: plane 127x50.2mm, normal (0,-1,0), area 6375.5mm2, adj f94,f115,f116,f118
  f120: plane 127x50.8mm, normal (-1,0,0), area 6451.6mm2, adj f121,f122,f123,f124
  f121: plane 56.26x50.8mm, normal (0,0,1), area 2757.8mm2, adj f94,f120,f122,f124
  f122: plane 127x50.2mm, normal (0,1,0), area 6375.5mm2, adj f94,f120,f121,f123
  f123: plane 56.26x50.8mm, normal (0,0,-1), area 2757.8mm2, adj f94,f120,f122,f124
  f124: plane 127x50.2mm, normal (0,-1,0), area 6375.5mm2, adj f94,f120,f121,f123
PLACE A t=(0,0,-2921)mm
PLACE B rot(axis=(0,0,1),180deg) t=(50.8,0,-2921)mm
MATE revolute B.f85 <-> A.f122  axis (0,0,1) through (-1625.6,0,-1333.5)mm
